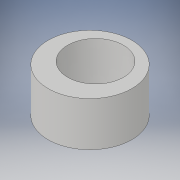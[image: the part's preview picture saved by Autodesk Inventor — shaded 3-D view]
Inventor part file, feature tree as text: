
AUTODESK INVENTOR PART (.ipt)
format: ipt  version: 2019 (Build 230136000, 136)  size: 96,256 bytes
history: native  units: in
note: dims shown in document units (in); Inventor stores cm internally (conversion verified against a paired STEP export)
features: extrude x1, sketch x1
ambient origin geometry x8: Origin, YZ Plane, XZ Plane, XY Plane, X Axis, Y Axis, Z Axis, Center Point
bodies: Solid1 (feature_tree)
feature tree (2):
  extrude  "Extrusion1"  Depth=0.25in
  sketch  "Sketch1"  dims[d0=0.4724in d1=0.315in d2=0.0312in d3=0.25in d4=0.0in]
